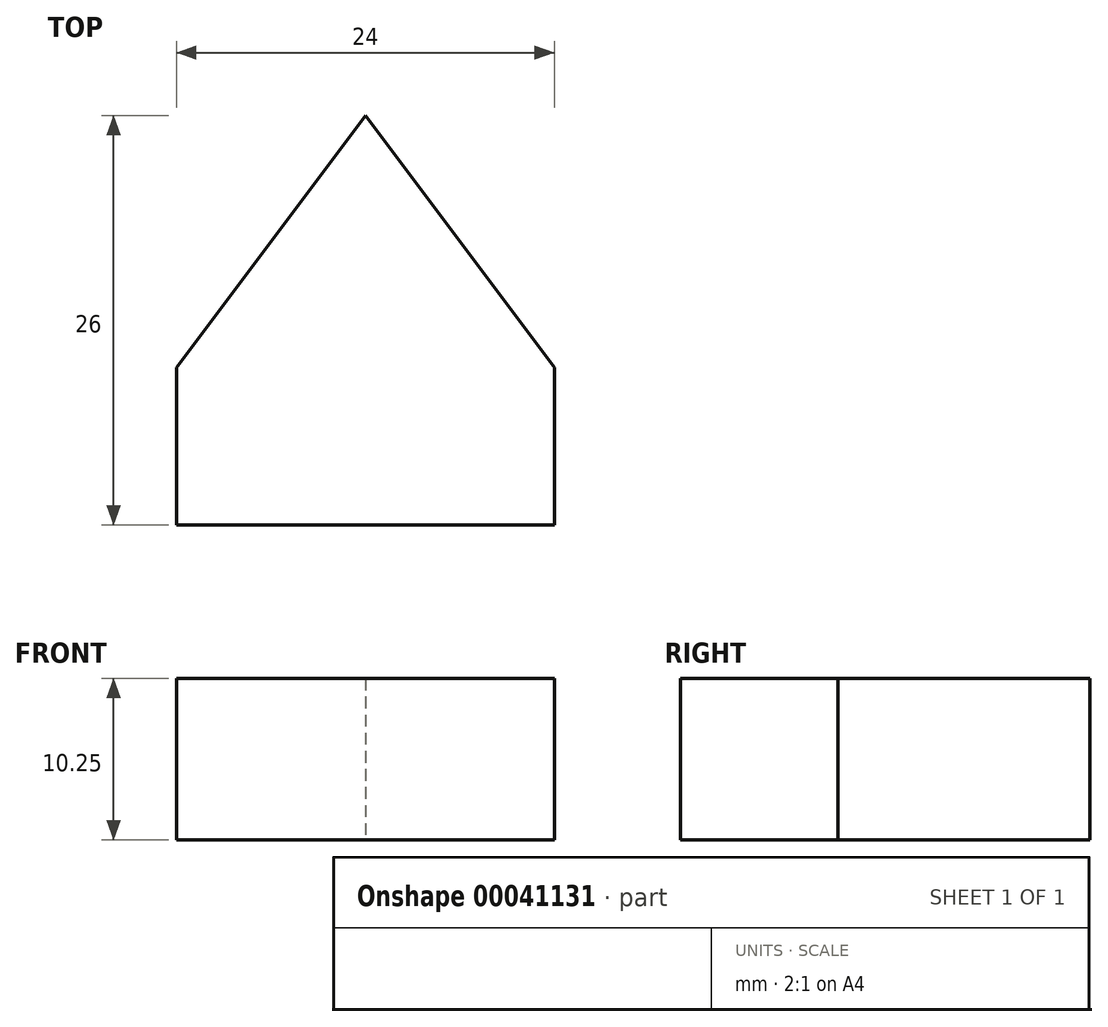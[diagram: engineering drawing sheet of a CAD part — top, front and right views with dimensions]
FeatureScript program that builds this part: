
annotation { "Feature Type Name" : "Feature", "Feature Type Description" : "" }
export const myFeature = defineFeature(function(context is Context, id is Id, definition is map)
    precondition{}
    {
        {
            var Q0;
            Q0=qCreatedBy(makeId("Top.planeOp"),FACE);
            var sketch = newSketch(context, id + "F0", { "sketchPlane" : qUnion([Q0])});
            skLineSegment(sketch, "E0.rect.bottom", {"start": v(12, 2.82) * mm, "end": v(-12, 2.82) * mm});
            skLineSegment(sketch, "E0.rect.top", {"start": v(12, -7.18) * mm, "end": v(-12, -7.18) * mm});
            skLineSegment(sketch, "E0.rect.left", {"start": v(12, 2.82) * mm, "end": v(12, -7.18) * mm});
            skLineSegment(sketch, "E0.rect.right", {"start": v(-12, 2.82) * mm, "end": v(-12, -7.18) * mm});
            skPoint(sketch, "E0.rect.middle", {"position": v(0, -2.18) * mm});
            skLineSegment(sketch, "E1", {"start": v(-12, 2.82) * mm, "end": v(0, 18.82) * mm});
            skLineSegment(sketch, "E2", {"start": v(12, 2.82) * mm, "end": v(0, 18.82) * mm});
            skSolve(sketch);
        }
        {
            var Q0;
            Q0=makeQuery(id+"F0.imprint","IMPRINT",FACE,{"disambiguationData":[TD([[makeQuery(id+"F0.imprint","IMPRINT",EDGE,{"derivedFrom":sQuery(id+"F0.wireOp",EDGE,"E0.rect.bottom")}),-1.0]])]});
            var Q1;
            Q1=makeQuery(id+"F0.imprint","IMPRINT",FACE,{"disambiguationData":[TD([[makeQuery(id+"F0.imprint","IMPRINT",EDGE,{"derivedFrom":sQuery(id+"F0.wireOp",EDGE,"E0.rect.bottom")}),1.0]])]});
            extrude(context, id + "F1", {"entities" : qUnion([Q0, Q1]), "depth" : 10.25 * mm});
        }
    });
